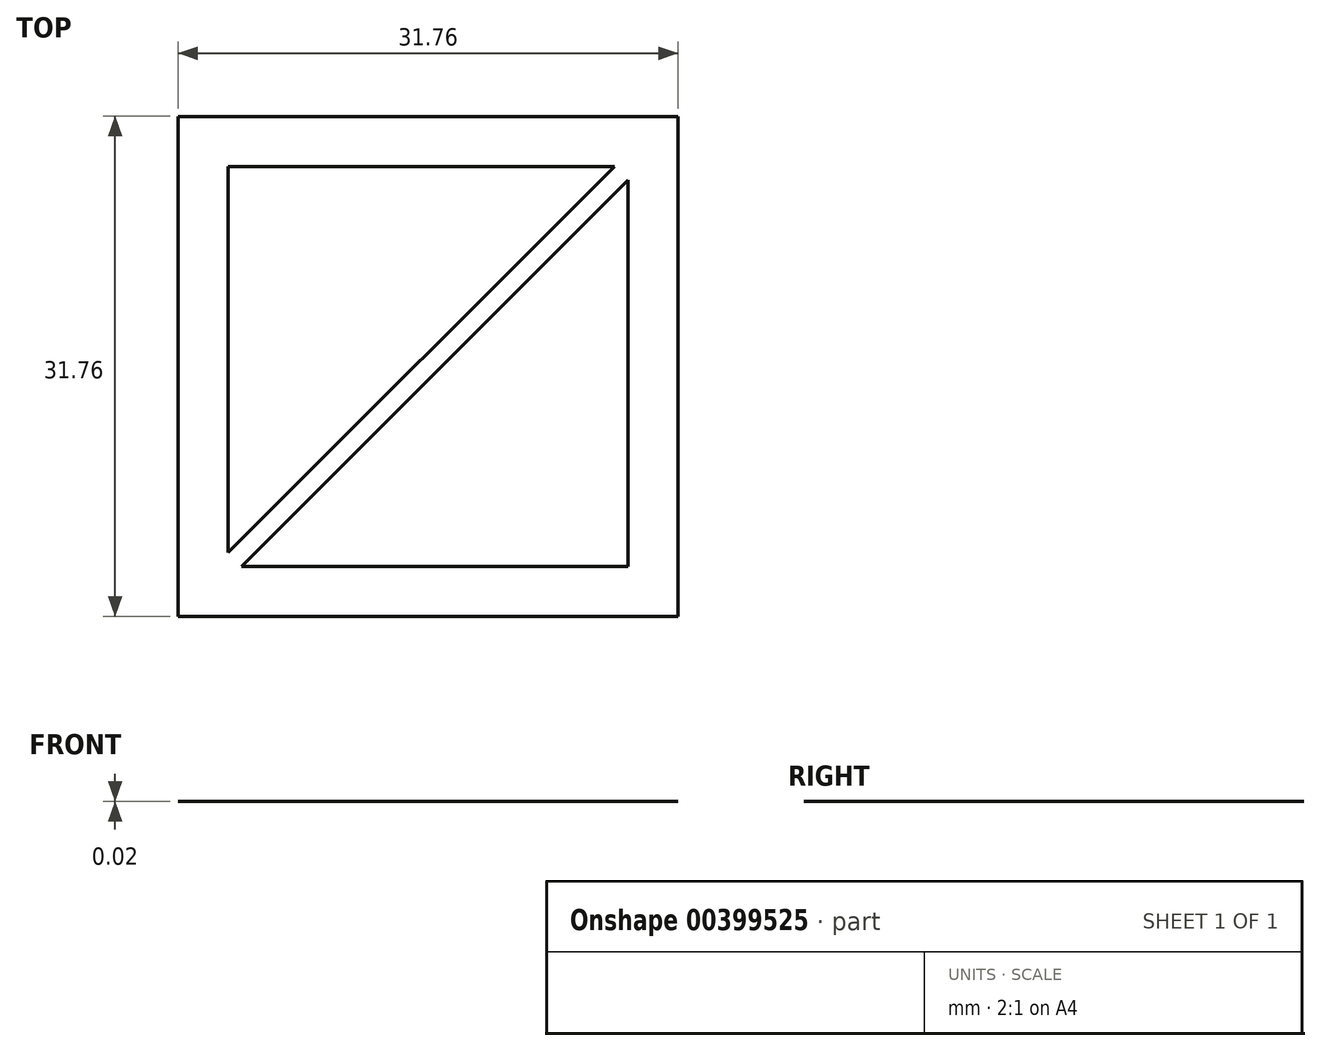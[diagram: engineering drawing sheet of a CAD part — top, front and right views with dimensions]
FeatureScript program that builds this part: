
annotation { "Feature Type Name" : "Feature", "Feature Type Description" : "" }
export const myFeature = defineFeature(function(context is Context, id is Id, definition is map)
    precondition{}
    {
        {
            var Q0;
            Q0=qCreatedBy(makeId("Top.planeOp"),FACE);
            var sketch = newSketch(context, id + "F0", { "sketchPlane" : qUnion([Q0])});
            skLineSegment(sketch, "E0.bottom", {"start": v(15.88, 15.88) * mm, "end": v(-15.88, 15.88) * mm});
            skLineSegment(sketch, "E0.top", {"start": v(15.88, -15.88) * mm, "end": v(-15.88, -15.88) * mm});
            skLineSegment(sketch, "E0.left", {"start": v(15.88, 15.88) * mm, "end": v(15.88, -15.88) * mm});
            skLineSegment(sketch, "E0.right", {"start": v(-15.88, 15.88) * mm, "end": v(-15.88, -15.88) * mm});
            skPoint(sketch, "E0.middle", {"position": v(0, 0) * mm});
            skSolve(sketch);
        }
        {
            var Q0;
            Q0 = qSketchRegion(id + "F0", true);
            extrude(context, id + "F1", {"entities" : qUnion([Q0]), "depth" : 1 / 203.2 * mm});
        }
        {
            var Q0;
            Q0=makeQuery(id+"F1.opExtrude","CAP_FACE",FACE,{"disambiguationData":[OSD([sQuery(id+"F0.wireOp",EDGE,"E0.bottom"),sQuery(id+"F0.wireOp",EDGE,"E0.top"),sQuery(id+"F0.wireOp",EDGE,"E0.left"),sQuery(id+"F0.wireOp",EDGE,"E0.right")])],"isStart":false});
            var sketch = newSketch(context, id + "F2", { "sketchPlane" : qUnion([Q0])});
            skLineSegment(sketch, "E1.0", {"start": v(12.7, -12.7) * mm, "end": v(-12.7, -12.7) * mm});
            skLineSegment(sketch, "E1.1", {"start": v(12.7, 12.7) * mm, "end": v(12.7, -12.7) * mm});
            skLineSegment(sketch, "E1.2", {"start": v(12.7, 12.7) * mm, "end": v(-12.7, 12.7) * mm});
            skLineSegment(sketch, "E1.3", {"start": v(-12.7, 12.7) * mm, "end": v(-12.7, -12.7) * mm});
            skLineSegment(sketch, "E2", {"start": v(12.7, 12.7) * mm, "end": v(-12.7, -12.7) * mm});
            skLineSegment(sketch, "E3", {"start": v(11.83, 12.7) * mm, "end": v(-12.7, -11.83) * mm});
            skLineSegment(sketch, "E4.MirrorCS", {"start": v(12.7, 11.83) * mm, "end": v(-11.83, -12.7) * mm});
            skSolve(sketch);
        }
        {
            var Q0;
            {var subQ0=sQuery(id+"F2.wireOp",EDGE,"E2");Q0=makeQuery(id+"F2.imprint","IMPRINT",FACE,{"disambiguationData":[TD([[makeQuery(id+"F2.imprint","IMPRINT",EDGE,{"derivedFrom":subQ0}),-1.0]])]});}
            var Q1;
            {var subQ0=sQuery(id+"F2.wireOp",EDGE,"E2");Q1=makeQuery(id+"F2.imprint","IMPRINT",FACE,{"disambiguationData":[TD([[makeQuery(id+"F2.imprint","IMPRINT",EDGE,{"derivedFrom":subQ0}),1.0]])]});}
            var Q2;
            Q2=makeQuery(id+"F2.imprint","IMPRINT",FACE,{"disambiguationData":[TD([[makeQuery(id+"F2.imprint","IMPRINT",EDGE,{"derivedFrom":makeQuery(id+"F1.opExtrude","CAP_EDGE",EDGE,{"disambiguationData":[OSD([sQuery(id+"F0.wireOp",EDGE,"E0.bottom")])],"isStart":false})}),1.0]])]});
            extrude(context, id + "F3", {"entities" : qUnion([Q0, Q1, Q2]), "operationType" : NewBodyOperationType.ADD, "depth" : 1 / 50.8 * mm});
        }
    });
